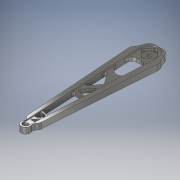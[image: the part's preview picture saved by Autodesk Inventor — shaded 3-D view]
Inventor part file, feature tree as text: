
AUTODESK INVENTOR PART (.ipt)
format: ipt  version: 2019.4 (Build 234330000, 330)  size: 655,872 bytes
history: native  units: mm
features: fillet x13, extrude x9, plane x8, sketch x8, other x2, pattern_circular x1, mirror x1
ambient origin geometry x8: Origin, YZ Plane, XZ Plane, XY Plane, X Axis, Y Axis, Z Axis, Center Point
bodies: Solid1 (feature_tree)
feature tree (42):
  other  "Delta_Arm"
  plane  "Work Plane6"
  plane  "Work Plane5"
  plane  "Work Plane7"
  plane  "Work Plane4"
  plane  "Work Plane1"
  plane  "Work Plane3"
  plane  "Work Plane2"
  extrude  "Extrusion8"  Depth=50.0mm
  extrude  "Extrusion9"  Depth=210.0mm
  extrude  "Extrusion11"  Depth=6.0mm
  plane  "Work Plane8"
  extrude  "Extrusion13"  Depth=10.0mm TaperAngle=0.0deg
  pattern_circular  "Circular Pattern1"  Count=21  [1 undecoded]
  extrude  "Extrusion14"  Depth=5.0mm TaperAngle=0.0deg
  mirror  "Mirror3"
  extrude  "Extrusion15"  Depth=3.0mm
  extrude  "Extrusion16"  Depth=40.0mm TaperAngle=360.0deg
  extrude  "Extrusion17"  Depth=10.0mm
  fillet  "Fillet4"  Radius=15.0mm
  fillet  "Fillet5"  Radius=2.0mm
  fillet  "Fillet6"  Radius=15.0mm
  fillet  "Fillet7"  Radius=20.0mm
  fillet  "Fillet8"  Radius=20.0mm
  fillet  "Fillet9"  Radius=6.0mm
  fillet  "Fillet10"  Radius=6.0mm
  fillet  "Fillet11"  Radius=30.0mm
  fillet  "Fillet12"  Radius=40.0mm
  fillet  "Fillet13"  Radius=10.0mm
  fillet  "Fillet14"  Radius=10.0mm
  fillet  "Fillet15"  Radius=3.0mm
  fillet  "Fillet16"  Radius=3.0mm
  extrude  "Extrusion18"  Depth=3.0mm
  sketch  "Sketch10"  dims[d0=20.0mm d2=50.0mm]
  sketch  "Sketch13"  dims[d44=5.0mm d50=210.0mm d51=210.0mm]
  sketch  "Sketch15"  dims[d52=10.0mm d53=0.0mm d54=6.0mm]
  sketch  "Sketch16"  dims[d55=6.0mm d56=10.0mm d57=0.0mm d63=210.0mm]
  sketch  "Sketch17"  dims[d64=25.0mm d65=5.0mm d66=0.0mm]
  sketch  "Sketch18"  dims[d70=-5.0mm d71=3.0mm]
  sketch  "Sketch19"  dims[d72=10.0mm d73=0.0mm d74=40.0mm d75=360.0deg]
  sketch  "Sketch20"  dims[d77=30.0mm d78=10.0mm d79=15.0mm d81=2.0mm d82=0.0mm d83=15.0mm d84=20.0mm d85=20.0mm d86=0.0mm d87=6.0mm d88=0.0mm d89=6.0mm d90=0.0mm d91=30.0mm d92=40.0mm d93=10.0mm d94=10.0mm d95=3.0mm d96=3.0mm d97=3.0mm d98=7.0mm d99=7.0mm d100=10.0mm d101=3.0mm d102=5.0mm d103=1.0mm d104=9.5mm d105=5.0mm d106=0.0mm]
  other  "MeshFeature1"
note: 1 required parameter value undecoded (feature->parameter linkage not recoverable at this tier; creation-order binding heuristic only, values carry confidence <= 0.55)
